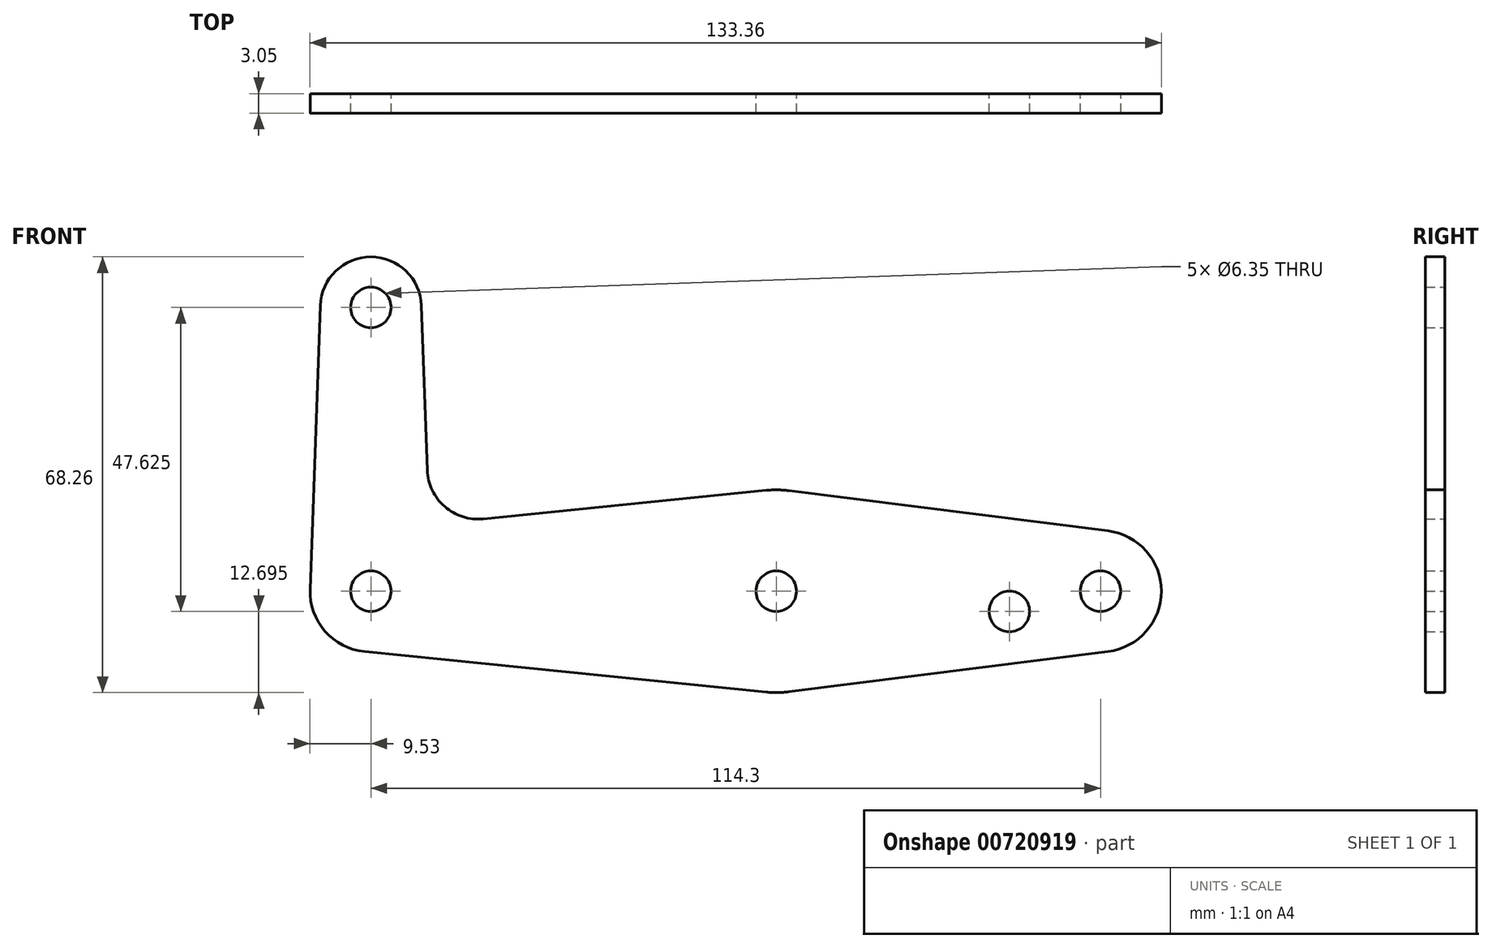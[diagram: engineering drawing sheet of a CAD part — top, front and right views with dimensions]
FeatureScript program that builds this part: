
annotation { "Feature Type Name" : "Feature", "Feature Type Description" : "" }
export const myFeature = defineFeature(function(context is Context, id is Id, definition is map)
    precondition{}
    {
        {
            var Q0;
            Q0=qCreatedBy(makeId("Front.planeOp"),FACE);
            var sketch = newSketch(context, id + "F0", { "sketchPlane" : qUnion([Q0])});
            skCircle(sketch, "E0", {"center": v(0, 0) * mm, "radius": 9.53 * mm});
            skCircle(sketch, "E1", {"center": v(63.5, 0) * mm, "radius": 15.88 * mm});
            skCircle(sketch, "E2", {"center": v(0, 44.45) * mm, "radius": 7.94 * mm});
            skCircle(sketch, "E3", {"center": v(114.3, 0) * mm, "radius": 9.53 * mm});
            skLineSegment(sketch, "E4", {"start": v(-7.93, 44.73) * mm, "end": v(-9.53, 0) * mm});
            skLineSegment(sketch, "E5", {"start": v(7.93, 44.73) * mm, "end": v(8.85, 18.97) * mm});
            skLineSegment(sketch, "E6", {"start": v(65.48, 15.75) * mm, "end": v(115.5, 9.45) * mm});
            skLineSegment(sketch, "E7", {"start": v(65.48, -15.75) * mm, "end": v(115.5, -9.45) * mm});
            skLineSegment(sketch, "E8", {"start": v(17.6, 11.34) * mm, "end": v(61.91, 15.8) * mm});
            skLineSegment(sketch, "E9", {"start": v(-0.95, -9.48) * mm, "end": v(61.91, -15.8) * mm});
            skCircle(sketch, "E10", {"center": v(0, 0) * mm, "radius": 3.18 * mm});
            skCircle(sketch, "E11", {"center": v(0, 44.45) * mm, "radius": 3.18 * mm});
            skCircle(sketch, "E12", {"center": v(63.5, 0) * mm, "radius": 3.18 * mm});
            skCircle(sketch, "E13", {"center": v(114.3, 0) * mm, "radius": 3.18 * mm});
            skPoint(sketch, "E14.newPointB", {"position": v(9.53, 0) * mm});
            skArc(sketch, "E14.filletArc", {"start": v(8.85, 18.97) * mm, "mid": v(11.57, 13.26) * mm, "end": v(17.6, 11.34) * mm});
            skLineSegment(sketch, "E15", {"start": v(0, 0) * mm, "end": v(114.3, 0) * mm});
            skCircle(sketch, "E16", {"center": v(100.03, -3.17) * mm, "radius": 3.18 * mm});
            skSolve(sketch);
        }
        {
            var Q0;
            Q0 = qSketchRegion(id + "F0", true);
            extrude(context, id + "F1", {"entities" : qUnion([Q0]), "depth" : 3.05 * mm, "offsetDistance" : 25.4 * mm});
        }
    });
